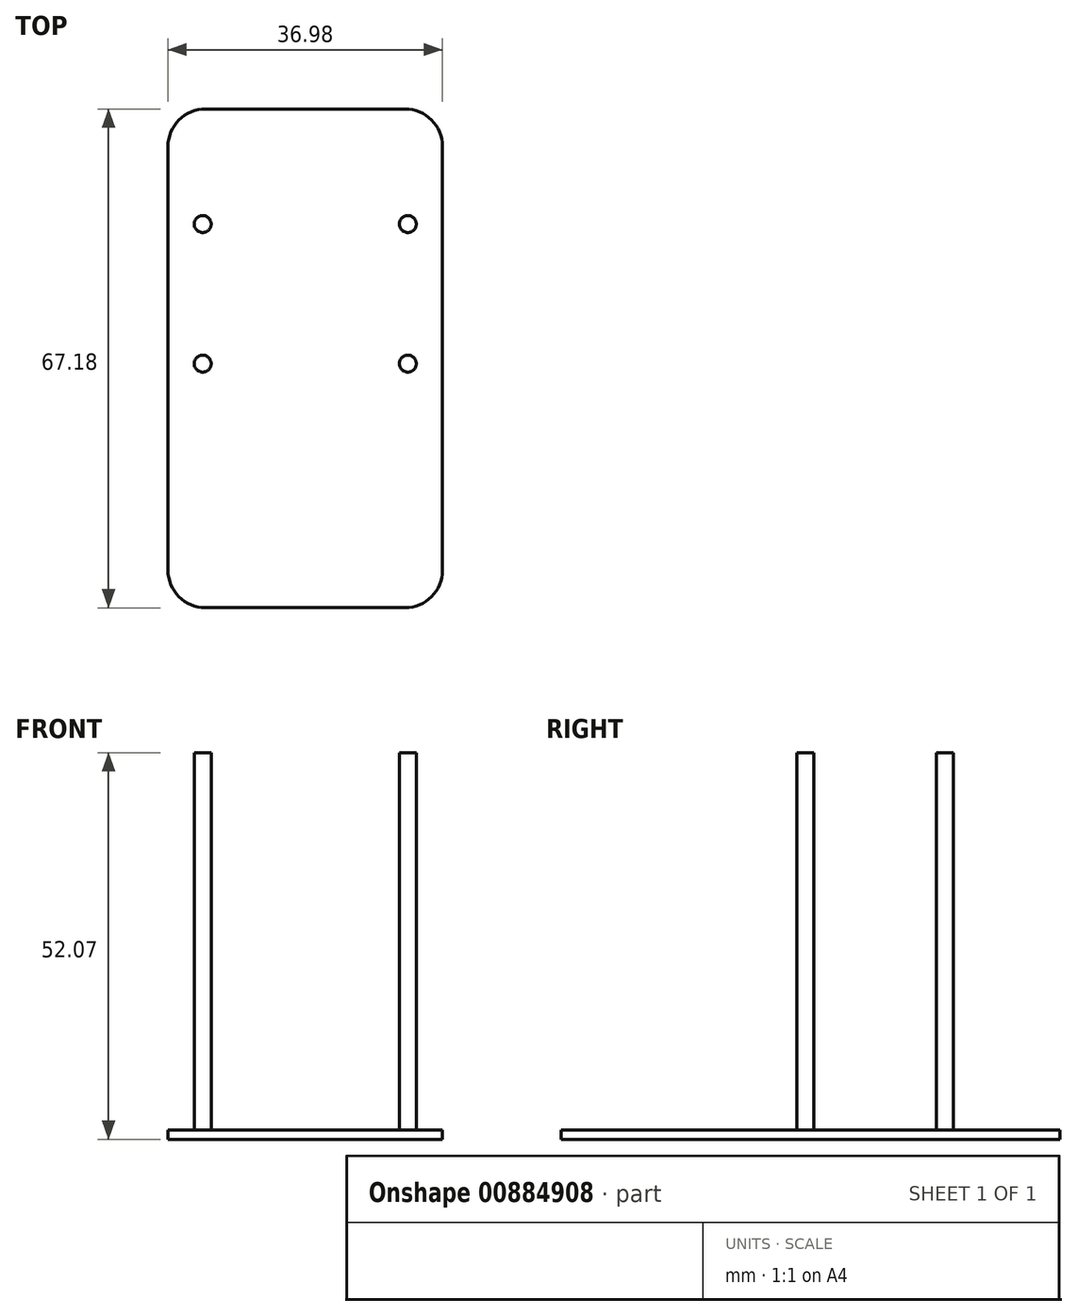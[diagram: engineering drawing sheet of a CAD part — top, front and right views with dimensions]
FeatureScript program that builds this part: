
annotation { "Feature Type Name" : "Feature", "Feature Type Description" : "" }
export const myFeature = defineFeature(function(context is Context, id is Id, definition is map)
    precondition{}
    {
        {
            var Q0;
            Q0=qCreatedBy(makeId("Top.planeOp"),FACE);
            var sketch = newSketch(context, id + "F0", { "sketchPlane" : qUnion([Q0])});
            skPoint(sketch, "E0.middle", {"position": v(0.34, -0.83) * mm});
            skCircle(sketch, "E1", {"center": v(-13.48, -10.23) * mm, "radius": 1.14 * mm});
            skCircle(sketch, "E2", {"center": v(-13.48, 8.57) * mm, "radius": 1.14 * mm});
            skCircle(sketch, "E3", {"center": v(14.16, 8.57) * mm, "radius": 1.14 * mm});
            skCircle(sketch, "E4", {"center": v(14.16, -10.23) * mm, "radius": 1.14 * mm});
            skLineSegment(sketch, "E5.bottom", {"start": v(13.75, 24.07) * mm, "end": v(-13.07, 24.07) * mm});
            skLineSegment(sketch, "E5.left", {"start": v(18.83, 18.99) * mm, "end": v(18.83, -20.64) * mm});
            skLineSegment(sketch, "E5.right", {"start": v(-18.15, 18.99) * mm, "end": v(-18.15, -20.64) * mm});
            skPoint(sketch, "E6.visualSharp", {"position": v(-18.15, 24.07) * mm});
            skArc(sketch, "E6.filletArc", {"start": v(-13.07, 24.07) * mm, "mid": v(-16.66, 22.58) * mm, "end": v(-18.15, 18.99) * mm});
            skPoint(sketch, "E7.visualSharp", {"position": v(18.83, -25.72) * mm});
            skPoint(sketch, "E8.visualSharp", {"position": v(-18.15, -25.72) * mm});
            skPoint(sketch, "E9.visualSharp", {"position": v(18.83, 24.07) * mm});
            skArc(sketch, "E9.filletArc", {"start": v(18.83, 18.99) * mm, "mid": v(17.34, 22.58) * mm, "end": v(13.75, 24.07) * mm});
            skLineSegment(sketch, "E10", {"start": v(-18.15, -20.64) * mm, "end": v(-18.15, -38.03) * mm});
            skLineSegment(sketch, "E11", {"start": v(18.83, -20.64) * mm, "end": v(18.83, -38.03) * mm});
            skLineSegment(sketch, "E12", {"start": v(-13.07, -43.1) * mm, "end": v(13.75, -43.1) * mm});
            skPoint(sketch, "E13.orphan", {"position": v(18.83, -45.14) * mm});
            skPoint(sketch, "E14.visualSharp", {"position": v(-18.15, -43.1) * mm});
            skArc(sketch, "E14.filletArc", {"start": v(-18.15, -38.03) * mm, "mid": v(-16.66, -41.62) * mm, "end": v(-13.07, -43.1) * mm});
            skPoint(sketch, "E15.visualSharp", {"position": v(18.83, -43.1) * mm});
            skArc(sketch, "E15.filletArc", {"start": v(13.75, -43.1) * mm, "mid": v(17.34, -41.62) * mm, "end": v(18.83, -38.03) * mm});
            skSolve(sketch);
        }
        {
            var Q0;
            Q0=makeQuery(id+"F0.imprint","IMPRINT",FACE,{"disambiguationData":[TD([[makeQuery(id+"F0.imprint","IMPRINT",EDGE,{"derivedFrom":sQuery(id+"F0.wireOp",EDGE,"E1")}),1.0]])]});
            var Q1;
            Q1=makeQuery(id+"F0.imprint","IMPRINT",FACE,{"disambiguationData":[TD([[makeQuery(id+"F0.imprint","IMPRINT",EDGE,{"derivedFrom":sQuery(id+"F0.wireOp",EDGE,"E2")}),1.0]])]});
            var Q2;
            Q2=makeQuery(id+"F0.imprint","IMPRINT",FACE,{"disambiguationData":[TD([[makeQuery(id+"F0.imprint","IMPRINT",EDGE,{"derivedFrom":sQuery(id+"F0.wireOp",EDGE,"E3")}),1.0]])]});
            var Q3;
            Q3=makeQuery(id+"F0.imprint","IMPRINT",FACE,{"disambiguationData":[TD([[makeQuery(id+"F0.imprint","IMPRINT",EDGE,{"derivedFrom":sQuery(id+"F0.wireOp",EDGE,"E4")}),1.0]])]});
            extrude(context, id + "F1", {"entities" : qUnion([Q0, Q1, Q2, Q3]), "depth" : 50.8 * mm, "offsetDistance" : 25.4 * mm});
        }
        {
            var Q0;
            Q0=makeQuery(id+"F0.imprint","IMPRINT",FACE,{"disambiguationData":[TD([[makeQuery(id+"F0.imprint","IMPRINT",EDGE,{"derivedFrom":sQuery(id+"F0.wireOp",EDGE,"E1")}),-1.0]])]});
            var Q1;
            Q1=makeQuery(id+"F0.imprint","IMPRINT",FACE,{"disambiguationData":[TD([[makeQuery(id+"F0.imprint","IMPRINT",EDGE,{"derivedFrom":sQuery(id+"F0.wireOp",EDGE,"E4")}),1.0]])]});
            var Q2;
            Q2=makeQuery(id+"F0.imprint","IMPRINT",FACE,{"disambiguationData":[TD([[makeQuery(id+"F0.imprint","IMPRINT",EDGE,{"derivedFrom":sQuery(id+"F0.wireOp",EDGE,"E1")}),1.0]])]});
            var Q3;
            Q3=makeQuery(id+"F0.imprint","IMPRINT",FACE,{"disambiguationData":[TD([[makeQuery(id+"F0.imprint","IMPRINT",EDGE,{"derivedFrom":sQuery(id+"F0.wireOp",EDGE,"E2")}),1.0]])]});
            var Q4;
            Q4=makeQuery(id+"F0.imprint","IMPRINT",FACE,{"disambiguationData":[TD([[makeQuery(id+"F0.imprint","IMPRINT",EDGE,{"derivedFrom":sQuery(id+"F0.wireOp",EDGE,"E3")}),1.0]])]});
            extrude(context, id + "F2", {"entities" : qUnion([Q0, Q1, Q2, Q3, Q4]), "oppositeDirection" : true, "depth" : 1.27 * mm, "offsetDistance" : 25.4 * mm});
        }
    });
